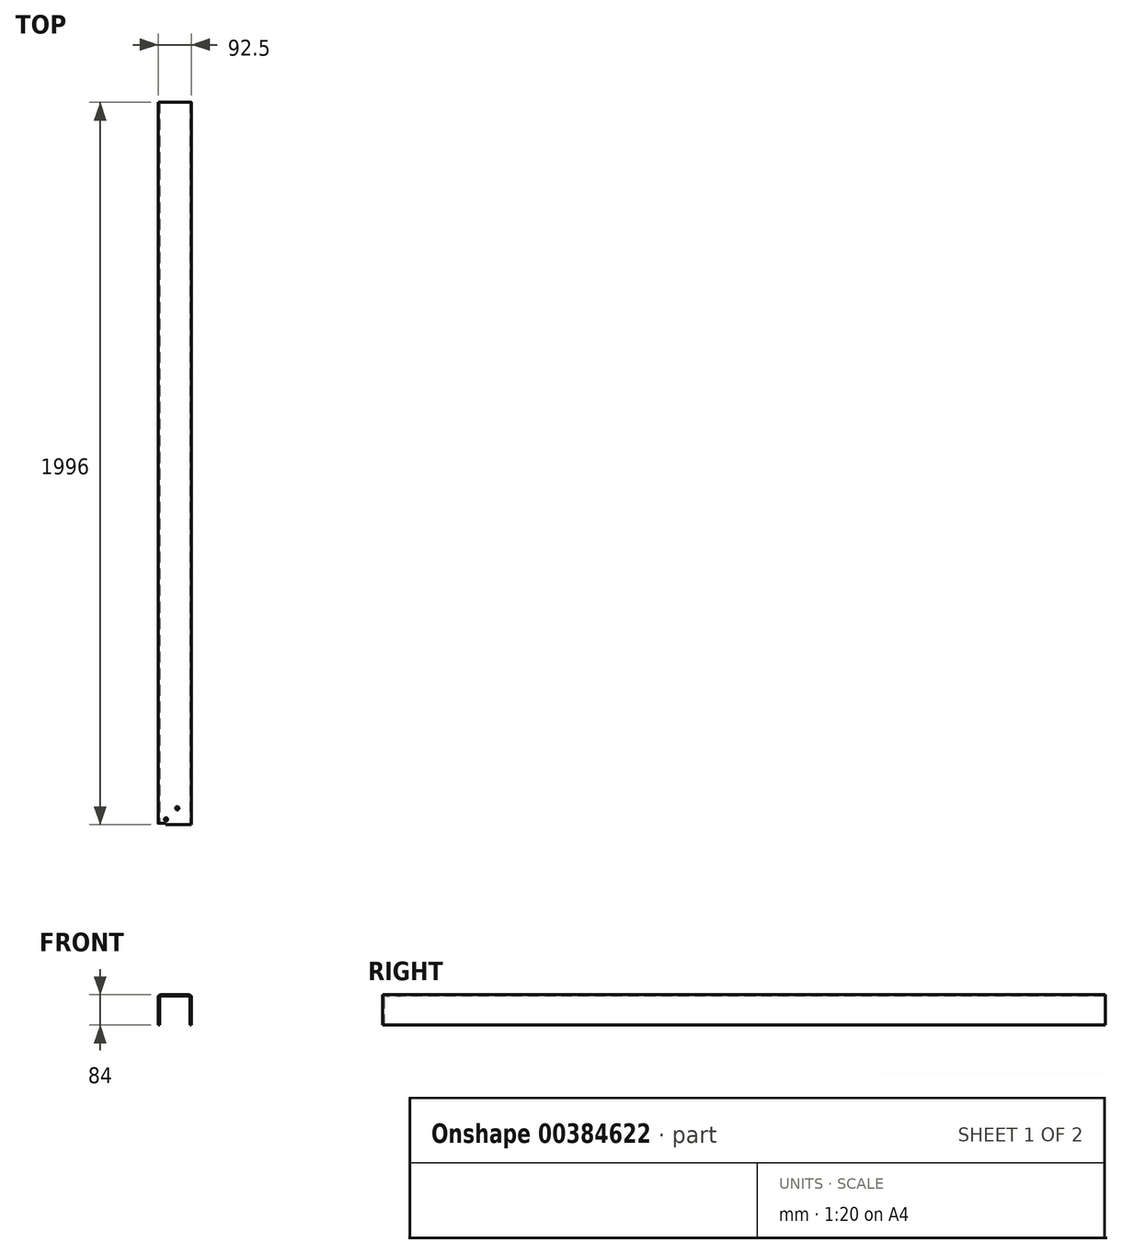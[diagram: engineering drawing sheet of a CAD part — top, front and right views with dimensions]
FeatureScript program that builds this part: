
annotation { "Feature Type Name" : "Feature", "Feature Type Description" : "" }
export const myFeature = defineFeature(function(context is Context, id is Id, definition is map)
    precondition{}
    {
        {
            var Q0;
            Q0=qCreatedBy(makeId("Front.planeOp"),FACE);
            var sketch = newSketch(context, id + "F0", { "sketchPlane" : qUnion([Q0])});
            skLineSegment(sketch, "E0.bottom", {"start": v(-46.25, -42) * mm, "end": v(-42.25, -42) * mm});
            skLineSegment(sketch, "E0.top", {"start": v(-38.25, 42) * mm, "end": v(38.25, 42) * mm});
            skLineSegment(sketch, "E0.left", {"start": v(-46.25, -42) * mm, "end": v(-46.25, 34) * mm});
            skLineSegment(sketch, "E0.right", {"start": v(46.25, -42) * mm, "end": v(46.25, 34) * mm});
            skPoint(sketch, "E0.middle", {"position": v(0, 0) * mm});
            skLineSegment(sketch, "E1", {"start": v(-42.25, -42) * mm, "end": v(-42.25, 34) * mm});
            skLineSegment(sketch, "E2", {"start": v(-38.25, 38) * mm, "end": v(38.25, 38) * mm});
            skLineSegment(sketch, "E3", {"start": v(42.25, 34) * mm, "end": v(42.25, -42) * mm});
            skLineSegment(sketch, "E4.trimOffspring", {"start": v(42.25, -42) * mm, "end": v(46.25, -42) * mm});
            skPoint(sketch, "E5.visualSharp", {"position": v(-42.25, 38) * mm});
            skArc(sketch, "E5.filletArc", {"start": v(-38.25, 38) * mm, "mid": v(-41.08, 36.83) * mm, "end": v(-42.25, 34) * mm});
            skPoint(sketch, "E6.visualSharp", {"position": v(42.25, 38) * mm});
            skArc(sketch, "E6.filletArc", {"start": v(42.25, 34) * mm, "mid": v(41.08, 36.83) * mm, "end": v(38.25, 38) * mm});
            skPoint(sketch, "E7.visualSharp", {"position": v(-46.25, 42) * mm});
            skArc(sketch, "E7.filletArc", {"start": v(-38.25, 42) * mm, "mid": v(-43.9, 39.66) * mm, "end": v(-46.25, 34) * mm});
            skPoint(sketch, "E8.visualSharp", {"position": v(46.25, 42) * mm});
            skArc(sketch, "E8.filletArc", {"start": v(46.25, 34) * mm, "mid": v(43.9, 39.66) * mm, "end": v(38.25, 42) * mm});
            skSolve(sketch);
        }
        {
            var Q0;
            Q0=makeQuery(id+"F0.imprint","IMPRINT",FACE,{"disambiguationData":[TD([[makeQuery(id+"F0.imprint","IMPRINT",EDGE,{"derivedFrom":sQuery(id+"F0.wireOp",EDGE,"E0.bottom")}),1.0]])]});
            extrude(context, id + "F1", {"entities" : qUnion([Q0]), "oppositeDirection" : true, "depth" : 1996 * mm});
        }
        {
            var Q0;
            Q0=qCreatedBy(makeId("Right.planeOp"),FACE);
            var Q1;
            Q1=makeQuery(id+"F1.opExtrude","CAP_EDGE",EDGE,{"disambiguationData":[OSD([sQuery(id+"F0.wireOp",EDGE,"E0.left")])],"isStart":true});
            cPlane(context, id + "F2", {"entities" : qUnion([Q0, Q1]), "cplaneType" : CPlaneType.LINE_ANGLE, "offset" : 25 * mm, "angle" : 0 * degree, "width" : 150 * mm, "height" : 150 * mm});
        }
        {
            var Q0;
            Q0=qCreatedBy(id+"F2.planeOp",FACE);
            var sketch = newSketch(context, id + "F3", { "sketchPlane" : qUnion([Q0])});
            skLineSegment(sketch, "E9.bottom", {"start": v(0, -43.13) * mm, "end": v(-4, -43.13) * mm});
            skLineSegment(sketch, "E9.top", {"start": v(0, 43.87) * mm, "end": v(-4, 43.87) * mm});
            skLineSegment(sketch, "E9.left", {"start": v(0, -43.13) * mm, "end": v(0, 43.87) * mm});
            skLineSegment(sketch, "E9.right", {"start": v(-4, -43.13) * mm, "end": v(-4, 43.87) * mm});
            skSolve(sketch);
        }
        {
            var Q0;
            Q0=makeQuery(id+"F3.imprint","IMPRINT",FACE,{"disambiguationData":[TD([[makeQuery(id+"F3.imprint","IMPRINT",EDGE,{"derivedFrom":sQuery(id+"F3.wireOp",EDGE,"E9.bottom")}),-1.0]])]});
            extrude(context, id + "F4", {"entities" : qUnion([Q0]), "operationType" : NewBodyOperationType.REMOVE, "oppositeDirection" : true, "depth" : 21.4 * mm});
        }
        {
            var Q0;
            Q0=makeQuery(id+"F1.opExtrude","SWEPT_FACE",FACE,{"disambiguationData":[OSD([sQuery(id+"F0.wireOp",EDGE,"E2")])]});
            var sketch = newSketch(context, id + "F5", { "sketchPlane" : qUnion([Q0])});
            skPoint(sketch, "E10.middle", {"position": v(0, 0) * mm});
            skLineSegment(sketch, "E11", {"start": v(-24.25, 0) * mm, "end": v(-24.25, -10) * mm});
            skLineSegment(sketch, "E12.bottom", {"start": v(-19.75, -14.5) * mm, "end": v(6.75, -14.5) * mm});
            skLineSegment(sketch, "E12.top", {"start": v(-24.25, -45.5) * mm, "end": v(2.25, -45.5) * mm});
            skLineSegment(sketch, "E12.left", {"start": v(-24.25, -19) * mm, "end": v(-24.25, -45.5) * mm});
            skLineSegment(sketch, "E12.right", {"start": v(6.75, -14.5) * mm, "end": v(6.75, -41) * mm});
            skCircle(sketch, "E13", {"center": v(-24.25, -14.5) * mm, "radius": 4.5 * mm});
            skCircle(sketch, "E14", {"center": v(6.75, -45.5) * mm, "radius": 4.5 * mm});
            skLineSegment(sketch, "E15", {"start": v(-24.25, 0) * mm, "end": v(-42.47, 0) * mm});
            skSolve(sketch);
        }
        {
            var Q0;
            {var subQ0=sQuery(id+"F5.wireOp",EDGE,"E13");var subQ1=makeQuery(id+"F5.imprint","IMPRINT",VERTEX,{"derivedFrom":subQ0});Q0=makeQuery(id+"F5.imprint","IMPRINT",FACE,{"disambiguationData":[TD([[makeQuery(id+"F5.imprint","IMPRINT",EDGE,{"disambiguationData":[TD([[subQ1,1.0]])],"derivedFrom":subQ0}),1.0]])]});}
            var Q1;
            {var subQ0=sQuery(id+"F5.wireOp",EDGE,"E14");var subQ1=makeQuery(id+"F5.imprint","INTERSECT",VERTEX,{"derivedFrom":[sQuery(id+"F5.wireOp",EDGE,"E12.top"),subQ0]});Q1=makeQuery(id+"F5.imprint","IMPRINT",FACE,{"disambiguationData":[TD([[makeQuery(id+"F5.imprint","IMPRINT",EDGE,{"disambiguationData":[TD([[subQ1,1.0]])],"derivedFrom":subQ0}),1.0]])]});}
            var Q2;
            Q2=sQuery(id+"F5.wireOp",EDGE,"E13");
            var Q3;
            Q3=sQuery(id+"F5.wireOp",EDGE,"E14");
            extrude(context, id + "F6", {"entities" : qUnion([Q0, Q1]), "operationType" : NewBodyOperationType.REMOVE, "surfaceEntities" : qUnion([Q2, Q3]), "endBound" : BoundingType.THROUGH_ALL, "oppositeDirection" : true, "depth" : 4 * mm});
        }
    });
